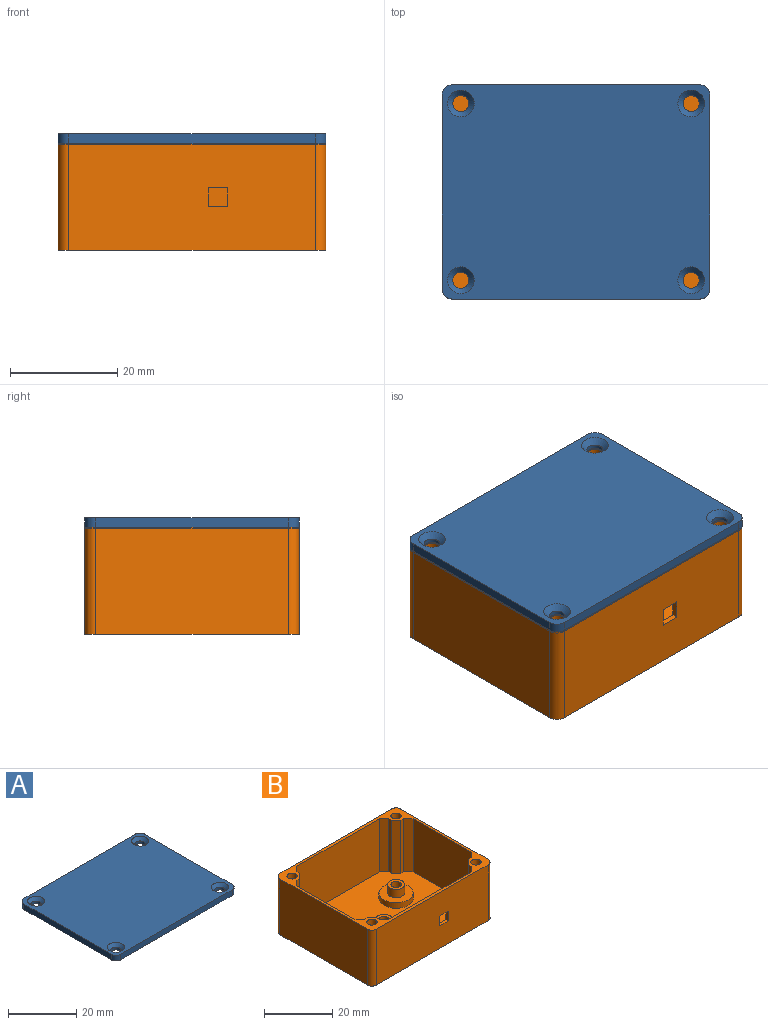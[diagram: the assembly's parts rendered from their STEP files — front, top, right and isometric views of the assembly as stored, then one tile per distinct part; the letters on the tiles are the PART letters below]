
ASSEMBLY  parts=2 mates=1
PART A: 18 faces, bbox 50x40x2 mm
  f0: plane 46x2mm, normal (0,1,0), area 92mm2, adj f4,f5,f14,f17
  f1: plane 36x2mm, normal (-1,0,0), area 72mm2, adj f4,f5,f14,f15
  f2: plane 46x2mm, normal (0,-1,0), area 92mm2, adj f4,f5,f15,f16
  f3: plane 36x2mm, normal (1,0,0), area 72mm2, adj f4,f5,f16,f17
  f4: plane 50x40mm, normal (0,0,1), area 1918mm2, adj f0,f1,f2,f3,f10,f11,f12,f13
  f5: plane 50x40mm, normal (0,0,-1), area 1968.3mm2, adj f0,f1,f2,f3,f6,f7,f8,f9
  f6: cylinder r=1.5mm len=3mm, axis (0,0,1), area 9.4mm2, adj f5,f12
  f7: cylinder r=1.5mm len=3mm, axis (0,0,1), area 9.4mm2, adj f5,f11
  f8: cylinder r=1.5mm len=3mm, axis (0,0,1), area 9.4mm2, adj f5,f10
  f9: cylinder r=1.5mm len=3mm, axis (0,0,1), area 9.4mm2, adj f5,f13
  f10: cone r=1.5mm half-angle=45deg, axis (0,0,1), area 17.8mm2, adj f4,f8
  f11: cone r=1.5mm half-angle=45deg, axis (0,0,1), area 17.8mm2, adj f4,f7
  f12: cone r=1.5mm half-angle=45deg, axis (0,0,1), area 17.8mm2, adj f4,f6
  f13: cone r=1.5mm half-angle=45deg, axis (0,0,1), area 17.8mm2, adj f4,f9
  f14: cylinder r=2mm len=2mm, axis (0,0,1), area 6.3mm2, adj f0,f1,f4,f5
  f15: cylinder r=2mm len=2mm, axis (0,0,-1), area 6.3mm2, adj f1,f2,f4,f5
  f16: cylinder r=2mm len=2mm, axis (0,0,1), area 6.3mm2, adj f2,f3,f4,f5
  f17: cylinder r=2mm len=2mm, axis (0,0,-1), area 6.3mm2, adj f0,f3,f4,f5
PART B: 71 faces, bbox 50x40x20 mm
  f0: plane 34x19mm, normal (0,1,0), area 633.4mm2, adj f5,f9,f56,f61,f67,f68,f69,f70
  f1: plane 46x20mm, normal (0,-1,0), area 907.4mm2, adj f2,f9,f52,f53,f67,f68,f69,f70
  f2: plane 50x40mm, normal (0,0,-1), area 1949.8mm2, adj f1,f10,f11,f12,f37,f38,f39,f40
  f3: cylinder r=1.5mm len=4mm, axis (0,0,-1), area 37.7mm2, adj f30,f50
  f4: cylinder r=1.5mm len=4mm, axis (0,0,-1), area 37.7mm2, adj f32,f43
  f5: plane 48x38mm, normal (0,0,1), area 1558.9mm2, adj f0,f6,f7,f8,f13,f14,f15,f16
  f6: plane 24x19mm, normal (-1,0,0), area 456mm2, adj f5,f9,f63,f64
  f7: plane 34x19mm, normal (0,-1,0), area 646mm2, adj f5,f9,f58,f66
  f8: plane 24x19mm, normal (1,0,0), area 456mm2, adj f5,f9,f55,f60
  f9: plane 50x40mm, normal (0,0,1), area 252.3mm2, adj f0,f1,f6,f7,f8,f10,f11,f12
  f10: plane 46x20mm, normal (0,1,0), area 920mm2, adj f2,f9,f51,f54
  f11: plane 36x20mm, normal (-1,0,0), area 720mm2, adj f2,f9,f51,f52
  f12: plane 36x20mm, normal (1,0,0), area 720mm2, adj f2,f9,f53,f54
  f13: plane 19x1mm, normal (0,-1,0), area 19mm2, adj f5,f9,f59,f60
  f14: plane 19x1mm, normal (1,0,0), area 19mm2, adj f5,f9,f58,f59
  f15: plane 19x1mm, normal (0,-1,0), area 19mm2, adj f5,f9,f64,f65
  f16: plane 19x1mm, normal (-1,0,0), area 19mm2, adj f5,f9,f65,f66
  f17: plane 19x1mm, normal (0,1,0), area 19mm2, adj f5,f9,f55,f57
  f18: plane 19x1mm, normal (1,0,0), area 19mm2, adj f5,f9,f56,f57
  f19: plane 19x1mm, normal (0,1,0), area 19mm2, adj f5,f9,f62,f63
  f20: plane 19x1mm, normal (-1,0,0), area 19mm2, adj f5,f9,f61,f62
  f21: cylinder r=1.5mm len=10mm, axis (0,0,1), area 94.2mm2, adj f9,f22
  f22: plane 3x3mm, normal (0,0,1), area 7.1mm2, adj f21
  f23: cylinder r=1.5mm len=10mm, axis (0,0,1), area 94.2mm2, adj f9,f24
  f24: plane 3x3mm, normal (0,0,1), area 7.1mm2, adj f23
  f25: cylinder r=1.5mm len=10mm, axis (0,0,1), area 94.2mm2, adj f9,f26
  f26: plane 3x3mm, normal (0,0,1), area 7.1mm2, adj f25
  f27: cylinder r=1.5mm len=10mm, axis (0,0,1), area 94.2mm2, adj f9,f28
  f28: plane 3x3mm, normal (0,0,1), area 7.1mm2, adj f27
  f29: cylinder r=2.5mm len=5mm, axis (0,0,-1), area 47.1mm2, adj f30,f34
  f30: plane 5x5mm, normal (0,0,1), area 12.6mm2, adj f3,f29
  f31: cylinder r=2.5mm len=5mm, axis (0,0,-1), area 47.1mm2, adj f32,f36
  f32: plane 5x5mm, normal (0,0,1), area 12.6mm2, adj f4,f31
  f33: cylinder r=5mm len=10mm, axis (0,0,-1), area 62.8mm2, adj f5,f34
  f34: plane 10x10mm, normal (0,0,1), area 58.9mm2, adj f29,f33
  f35: cylinder r=5mm len=10mm, axis (0,0,-1), area 62.8mm2, adj f5,f36
  f36: plane 10x10mm, normal (0,0,1), area 58.9mm2, adj f31,f35
  f37: plane 2.97x2mm, normal (-0.99,0.13,0), area 6mm2, adj f2,f38,f42,f43
  f38: plane 2.78x2mm, normal (-0.38,0.93,0), area 6mm2, adj f2,f37,f39,f43
  f39: plane 2.37x2mm, normal (0.61,0.79,0), area 6mm2, adj f2,f38,f40,f43
  f40: plane 2.97x2mm, normal (0.99,-0.13,0), area 6mm2, adj f2,f39,f41,f43
  f41: plane 2.78x2mm, normal (0.38,-0.93,0), area 6mm2, adj f2,f40,f42,f43
  f42: plane 2.37x2mm, normal (-0.61,-0.79,0), area 6mm2, adj f2,f37,f41,f43
  f43: plane 5.95x5.55mm, normal (0,0,-1), area 16.3mm2, adj f4,f37,f38,f39,f40,f41,f42
  f44: plane 2.98x2mm, normal (-0.99,-0.11,0), area 6mm2, adj f2,f45,f49,f50
  f45: plane 2.42x2mm, normal (-0.59,0.81,0), area 6mm2, adj f2,f44,f46,f50
  f46: plane 2.75x2mm, normal (0.4,0.92,0), area 6mm2, adj f2,f45,f47,f50
  f47: plane 2.98x2mm, normal (0.99,0.11,0), area 6mm2, adj f2,f46,f48,f50
  f48: plane 2.42x2mm, normal (0.59,-0.81,0), area 6mm2, adj f2,f47,f49,f50
  f49: plane 2.75x2mm, normal (-0.4,-0.92,0), area 6mm2, adj f2,f44,f48,f50
  f50: plane 5.96x5.49mm, normal (0,0,-1), area 16.3mm2, adj f3,f44,f45,f46,f47,f48,f49
  f51: cylinder r=2mm len=20mm, axis (0,0,1), area 62.8mm2, adj f2,f9,f10,f11
  f52: cylinder r=2mm len=20mm, axis (0,0,-1), area 62.8mm2, adj f1,f2,f9,f11
  f53: cylinder r=2mm len=20mm, axis (0,0,1), area 62.8mm2, adj f1,f2,f9,f12
  f54: cylinder r=2mm len=20mm, axis (0,0,-1), area 62.8mm2, adj f2,f9,f10,f12
  f55: plane 19x2mm, normal (0.71,0.71,0), area 53.7mm2, adj f5,f8,f9,f17
  f56: plane 19x2mm, normal (0.71,0.71,0), area 53.7mm2, adj f0,f5,f9,f18
  f57: plane 19x2mm, normal (0.71,0.71,0), area 53.7mm2, adj f5,f9,f17,f18
  f58: plane 19x2mm, normal (0.71,-0.71,0), area 53.7mm2, adj f5,f7,f9,f14
  f59: plane 19x2mm, normal (0.71,-0.71,0), area 53.7mm2, adj f5,f9,f13,f14
  f60: plane 19x2mm, normal (0.71,-0.71,0), area 53.7mm2, adj f5,f8,f9,f13
  f61: plane 19x2mm, normal (-0.71,0.71,0), area 53.7mm2, adj f0,f5,f9,f20
  f62: plane 19x2mm, normal (-0.71,0.71,0), area 53.7mm2, adj f5,f9,f19,f20
  f63: plane 19x2mm, normal (-0.71,0.71,0), area 53.7mm2, adj f5,f6,f9,f19
  f64: plane 19x2mm, normal (-0.71,-0.71,0), area 53.7mm2, adj f5,f6,f9,f15
  f65: plane 19x2mm, normal (-0.71,-0.71,0), area 53.7mm2, adj f5,f9,f15,f16
  f66: plane 19x2mm, normal (-0.71,-0.71,0), area 53.7mm2, adj f5,f7,f9,f16
  f67: plane 3.56x1mm, normal (0,0,-1), area 3.6mm2, adj f0,f1,f68,f70
  f68: plane 3.54x1mm, normal (1,0,0), area 3.5mm2, adj f0,f1,f67,f69
  f69: plane 3.56x1mm, normal (0,0,1), area 3.6mm2, adj f0,f1,f68,f70
  f70: plane 3.54x1mm, normal (-1,0,0), area 3.5mm2, adj f0,f1,f67,f69
PLACE A t=(-84.31,-29.37,40.96)mm
PLACE B t=(-14.49,-23.02,21.21)mm fixed
MATE slider B.f27 <-> A.f7  axis (0,0,1) through (-31.4,1.72,41.21)mm
